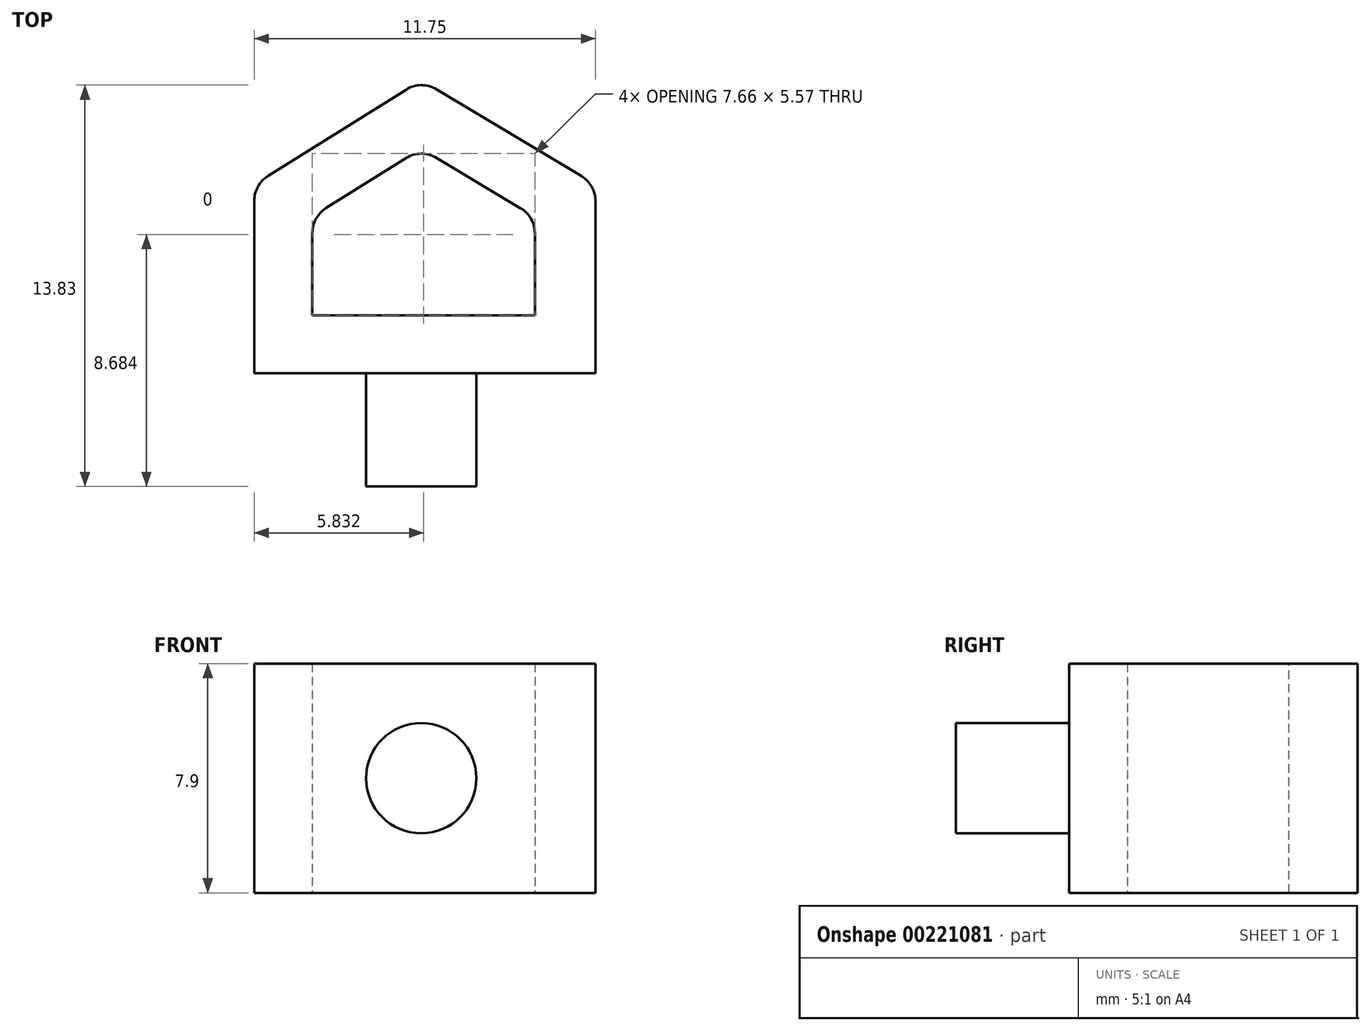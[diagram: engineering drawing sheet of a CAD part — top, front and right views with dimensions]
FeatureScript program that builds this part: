
annotation { "Feature Type Name" : "Feature", "Feature Type Description" : "" }
export const myFeature = defineFeature(function(context is Context, id is Id, definition is map)
    precondition{}
    {
        {
            var Q0;
            Q0=qCreatedBy(makeId("Top.planeOp"),FACE);
            var sketch = newSketch(context, id + "F0", { "sketchPlane" : qUnion([Q0])});
            skLineSegment(sketch, "E0", {"start": v(0, 0) * mm, "end": v(6, 0) * mm});
            skLineSegment(sketch, "E1", {"start": v(0, 0) * mm, "end": v(-5.75, 0) * mm});
            skLineSegment(sketch, "E2", {"start": v(-5.75, 0) * mm, "end": v(-5.75, 6.5) * mm});
            skLineSegment(sketch, "E3", {"start": v(6, 0) * mm, "end": v(6, 6.5) * mm});
            skLineSegment(sketch, "E4", {"start": v(0, 0) * mm, "end": v(0, 10.1) * mm});
            skLineSegment(sketch, "E5", {"start": v(0, 10.1) * mm, "end": v(6, 6.5) * mm});
            skLineSegment(sketch, "E6", {"start": v(-5.75, 6.5) * mm, "end": v(0, 10.1) * mm});
            skLineSegment(sketch, "E7.2", {"start": v(0, 2) * mm, "end": v(-3.75, 2) * mm});
            skLineSegment(sketch, "E8", {"start": v(-3.75, 5.4) * mm, "end": v(0, 7.74) * mm});
            skLineSegment(sketch, "E9", {"start": v(0, 7.74) * mm, "end": v(3.91, 5.4) * mm});
            skLineSegment(sketch, "E10", {"start": v(3.91, 5.4) * mm, "end": v(3.91, 2) * mm});
            skLineSegment(sketch, "E11", {"start": v(3.91, 2) * mm, "end": v(0, 2) * mm});
            skLineSegment(sketch, "E12", {"start": v(-3.75, 5.4) * mm, "end": v(-3.75, 2) * mm});
            skSolve(sketch);
        }
        {
            var Q0;
            Q0 = qSketchRegion(id + "F0", true);
            extrude(context, id + "F1", {"entities" : qUnion([Q0]), "endBound" : BoundingType.SYMMETRIC, "depth" : 7.9 * mm});
        }
        {
            var Q0;
            Q0=makeQuery(id+"F1.opExtrude","SWEPT_FACE",FACE,{"disambiguationData":[OSD([sQuery(id+"F0.wireOp",EDGE,"E0"),sQuery(id+"F0.wireOp",EDGE,"E1")])]});
            var sketch = newSketch(context, id + "F2", { "sketchPlane" : qUnion([Q0])});
            skCircle(sketch, "E13", {"center": v(0, 0) * mm, "radius": 1.9 * mm});
            skSolve(sketch);
        }
        {
            var Q0;
            Q0=makeQuery(id+"F2.imprint","IMPRINT",FACE,{"disambiguationData":[TD([[makeQuery(id+"F2.imprint","IMPRINT",EDGE,{"derivedFrom":sQuery(id+"F2.wireOp",EDGE,"E13")}),1.0]])]});
            var Q1;
            Q1=sQuery(id+"F2.wireOp",EDGE,"E13");
            extrude(context, id + "F3", {"entities" : qUnion([Q0]), "surfaceEntities" : qUnion([Q1]), "depth" : 3.9 * mm});
        }
        {
            var Q0;
            Q0=makeQuery(id+"F1.opExtrude","SWEPT_EDGE",EDGE,{"disambiguationData":[OSD([sQuery(id+"F0.wireOp",EDGE,"E4"),sQuery(id+"F0.wireOp",EDGE,"E5"),sQuery(id+"F0.wireOp",EDGE,"E6")])]});
            var Q1;
            Q1=makeQuery(id+"F1.opExtrude","SWEPT_EDGE",EDGE,{"disambiguationData":[OSD([sQuery(id+"F0.wireOp",EDGE,"E2"),sQuery(id+"F0.wireOp",EDGE,"E6")])]});
            var Q2;
            Q2=makeQuery(id+"F1.opExtrude","SWEPT_EDGE",EDGE,{"disambiguationData":[OSD([sQuery(id+"F0.wireOp",EDGE,"E3"),sQuery(id+"F0.wireOp",EDGE,"E5")])]});
            var Q3;
            Q3=makeQuery(id+"F1.opExtrude","SWEPT_EDGE",EDGE,{"disambiguationData":[OSD([sQuery(id+"F0.wireOp",EDGE,"E8"),sQuery(id+"F0.wireOp",EDGE,"E12")])]});
            var Q4;
            Q4=makeQuery(id+"F1.opExtrude","SWEPT_EDGE",EDGE,{"disambiguationData":[OSD([sQuery(id+"F0.wireOp",EDGE,"E9"),sQuery(id+"F0.wireOp",EDGE,"E10")])]});
            var Q5;
            Q5=makeQuery(id+"F1.opExtrude","SWEPT_EDGE",EDGE,{"disambiguationData":[OSD([sQuery(id+"F0.wireOp",EDGE,"E4"),sQuery(id+"F0.wireOp",EDGE,"E8"),sQuery(id+"F0.wireOp",EDGE,"E9")])]});
            fillet(context, id + "F4", {"entities" : qUnion([Q0, Q1, Q2, Q3, Q4, Q5]), "radius" : 1 * mm, "tangentPropagation" : true, "allowEdgeOverflow" : false});
        }
    });
